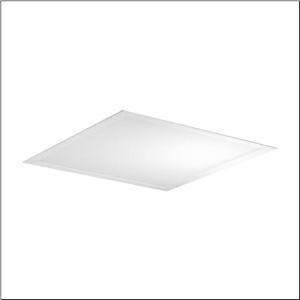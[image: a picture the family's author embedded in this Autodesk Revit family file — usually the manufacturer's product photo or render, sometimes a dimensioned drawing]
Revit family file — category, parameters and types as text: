
# Revit family: apollon_r__31_square_51mp11wd2442_8a23
name_source: partatom
category: Lighting Fixtures
units: mm (PartAtom-declared; Revit-internal decimal feet)

## family parameters
Cut with Voids When Loaded = No
Host = Face
Light Source = No
Part Type = Normal
Room Calculation Point = No
Round Connector Dimension = Use Diameter
Shared = No

## types (1)
- Apollon® 31 square (1 x LED, 4000 lm, 27.5 W, 4000K)
    Apparent Load = 28 VA
    CIE Flux Codes = 61 87 97 100 100
    Color Rendering = 80
    Color Temperature = 4000K
    Default Elevation = 1800 mm
    Description = Apollon® 31 square, office luminaire, primary optical cover: micro prismatic cover, of PMMA, CAT 2 (L<= 3000cd/m²), light emission: direct distribution, primary light characteristic: symmetric, installation type: lay-in mounting, LED, rated luminous flux: 4.000lm, luminous efficacy: 145lm/W, light colour: 840, colour temperature: 4000K, with terminal, 5-pole, mains connection: 220..240V, AC/DC, 0/50..60Hz, rated input power: 28W, housing, of aluminium, traffic white (RAL 9016), module: M625, length: 620mm, width: 620mm, height: 32mm, housing upper side, of sheet steel, galvanised, protection rating (complete): IP20, protection rating (on room side): IP40, insulation class (complete): insulation class II (safety insulation), certification: CE, ENEC, impact resistance: IK03, permissible operating ambient temperature: -20..+40°C, permissible storage temperature: -20..+60°C, packaging unit: 1 piece
    Height = 0 mm  [stored 0 ft]
    Lamp = 1 x LED
    Lamp Light Flux = 4000 lm
    Lamp Power = 27.5 W
    Lamp count = 1
    Length = 620 mm
    Luminous efficacy = 145 lm/W
    Manufacturer = Siteco
    ModVariant = No
    Model = 51MP11WD2442
    Mounting Place = Ceiling
    Mounting Type = Recessed
    Number of Poles = 1
    OnlyDefault = Yes
    Power Factor = 1
    Product Name = Apollon® 31 square
    Product group = office luminaire | ceiling recessed
    ProductGroupID = 401
    Protection Class = Protection class II
    Protection Degree = IP 20
    RLX_Detail_Level = 1
    RLX_Emergency_Light_Flux = 0 lm
    RLX_Emergency_Type = 0
    RLX_Emergency_Type_DB = No
    RlxData = <blob elided: 12941 chars, md5=328001f2>
    Socket = socket
    Standby Power = 0 W
    System Light Flux = 4000 lm
    System Power = 28 W
    Type Comments = Product without accessories
    Type Image = l_1291039.jpg
    URL = http://relux.com
    VarID = ---
    Voltage = 0 V
    Weight = 0.00 kg
    Width = 620 mm

note: [stored X ft] marks values corroborated as IEEE doubles in the binary element streams (Revit-internal decimal feet)

## geometry (parser evidence)
native form markers: Sweep x10
no freeform markers — native parametric forms only
